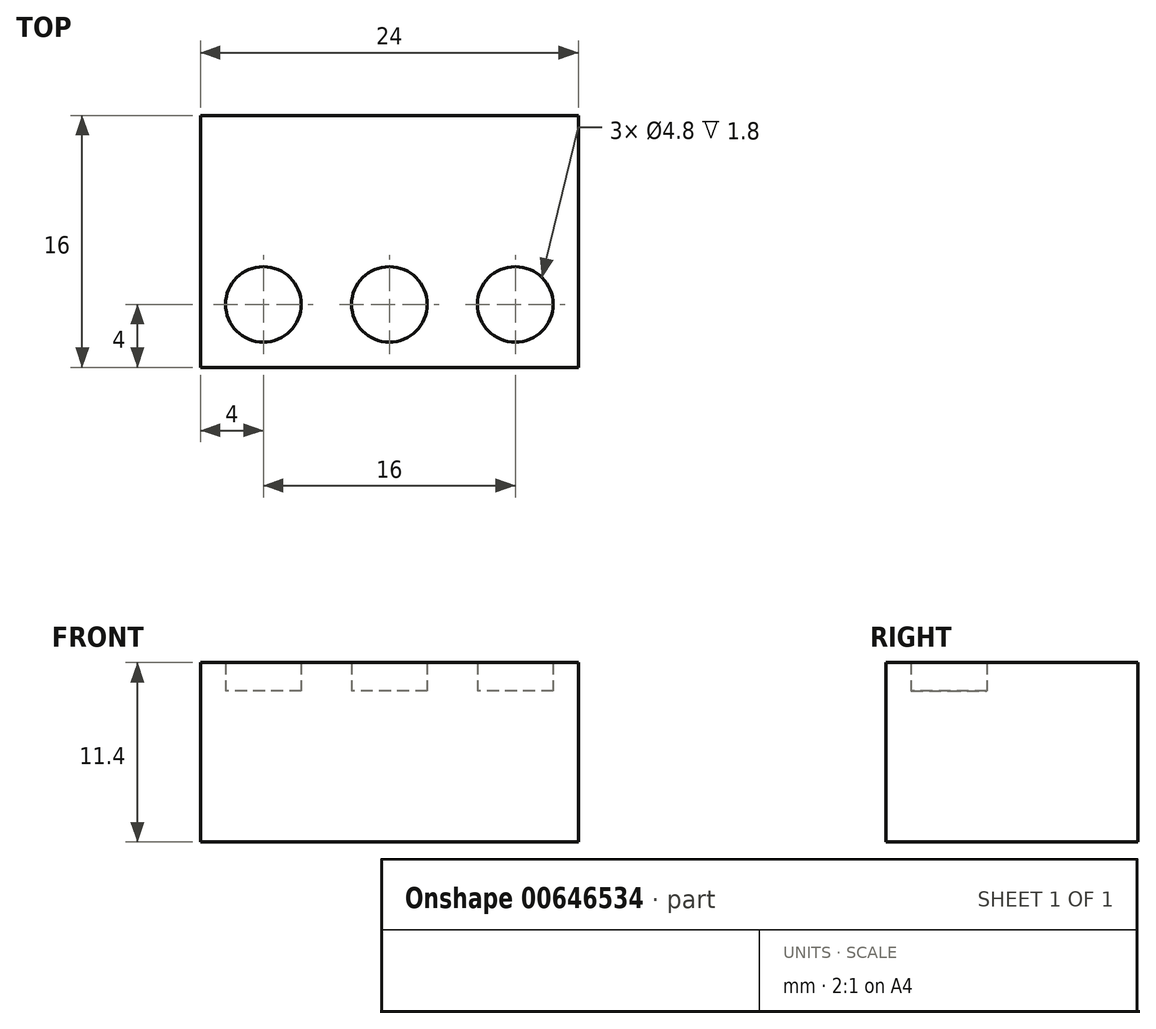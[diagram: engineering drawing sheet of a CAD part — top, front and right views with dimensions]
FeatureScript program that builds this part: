
annotation { "Feature Type Name" : "Feature", "Feature Type Description" : "" }
export const myFeature = defineFeature(function(context is Context, id is Id, definition is map)
    precondition{}
    {
        {
            var Q0;
            Q0=qCreatedBy(makeId("Top.planeOp"),FACE);
            var sketch = newSketch(context, id + "F0", { "sketchPlane" : qUnion([Q0])});
            skLineSegment(sketch, "E0.bottom", {"start": v(0, 0) * mm, "end": v(-24, 0) * mm});
            skLineSegment(sketch, "E0.top", {"start": v(0, 16) * mm, "end": v(-24, 16) * mm});
            skLineSegment(sketch, "E0.left", {"start": v(0, 0) * mm, "end": v(0, 16) * mm});
            skLineSegment(sketch, "E0.right", {"start": v(-24, 0) * mm, "end": v(-24, 16) * mm});
            skSolve(sketch);
        }
        {
            var Q0;
            Q0 = qSketchRegion(id + "F0", true);
            extrude(context, id + "F1", {"entities" : qUnion([Q0]), "depth" : 9.6 * mm, "offsetDistance" : 25.4 * mm});
        }
        {
            var Q0;
            Q0=makeQuery(id+"F1.opExtrude","CAP_FACE",FACE,{"disambiguationData":[OSD([sQuery(id+"F0.wireOp",EDGE,"E0.bottom"),sQuery(id+"F0.wireOp",EDGE,"E0.top"),sQuery(id+"F0.wireOp",EDGE,"E0.left"),sQuery(id+"F0.wireOp",EDGE,"E0.right")])],"isStart":false});
            var sketch = newSketch(context, id + "F2", { "sketchPlane" : qUnion([Q0])});
            skLineSegment(sketch, "E1", {"start": v(-24, 8) * mm, "end": v(0, 8) * mm, "construction": true});
            skLineSegment(sketch, "E2", {"start": v(-16, 16) * mm, "end": v(-16, 0) * mm, "construction": true});
            skLineSegment(sketch, "E3", {"start": v(-8, 16) * mm, "end": v(-8, 0) * mm, "construction": true});
            skLineSegment(sketch, "E4", {"start": v(-24, 16) * mm, "end": v(-16, 8) * mm, "construction": true});
            skLineSegment(sketch, "E5", {"start": v(-16, 8) * mm, "end": v(-8, 16) * mm, "construction": true});
            skLineSegment(sketch, "E6", {"start": v(-8, 16) * mm, "end": v(0, 8) * mm, "construction": true});
            skCircle(sketch, "E7", {"center": v(-20, 12) * mm, "radius": 2.4 * mm});
            skCircle(sketch, "E8", {"center": v(-12, 12) * mm, "radius": 2.4 * mm});
            skCircle(sketch, "E9", {"center": v(-4, 12) * mm, "radius": 2.4 * mm});
            skCircle(sketch, "E10.MirrorC", {"center": v(-20, 4) * mm, "radius": 2.4 * mm});
            skCircle(sketch, "E11.MirrorC", {"center": v(-12, 4) * mm, "radius": 2.4 * mm});
            skCircle(sketch, "E12.MirrorC", {"center": v(-4, 4) * mm, "radius": 2.4 * mm});
            skSolve(sketch);
        }
        {
            var Q0;
            Q0=makeQuery(id+"F2.imprint","IMPRINT",FACE,{"disambiguationData":[TD([[makeQuery(id+"F2.imprint","IMPRINT",EDGE,{"derivedFrom":sQuery(id+"F2.wireOp",EDGE,"E7")}),1.0]])]});
            var Q1;
            Q1=makeQuery(id+"F2.imprint","IMPRINT",FACE,{"disambiguationData":[TD([[makeQuery(id+"F2.imprint","IMPRINT",EDGE,{"derivedFrom":sQuery(id+"F2.wireOp",EDGE,"E8")}),1.0]])]});
            var Q2;
            Q2=makeQuery(id+"F2.imprint","IMPRINT",FACE,{"disambiguationData":[TD([[makeQuery(id+"F2.imprint","IMPRINT",EDGE,{"derivedFrom":sQuery(id+"F2.wireOp",EDGE,"E9")}),1.0]])]});
            var Q3;
            Q3=makeQuery(id+"F2.imprint","IMPRINT",FACE,{"disambiguationData":[TD([[makeQuery(id+"F2.imprint","IMPRINT",EDGE,{"derivedFrom":sQuery(id+"F2.wireOp",EDGE,"E11.MirrorC")}),-1.0]])]});
            var Q4;
            Q4=makeQuery(id+"F2.imprint","IMPRINT",FACE,{"disambiguationData":[TD([[makeQuery(id+"F2.imprint","IMPRINT",EDGE,{"derivedFrom":sQuery(id+"F2.wireOp",EDGE,"E12.MirrorC")}),-1.0]])]});
            var Q5;
            Q5=makeQuery(id+"F2.imprint","IMPRINT",FACE,{"disambiguationData":[TD([[makeQuery(id+"F2.imprint","IMPRINT",EDGE,{"derivedFrom":sQuery(id+"F2.wireOp",EDGE,"E10.MirrorC")}),-1.0]])]});
            extrude(context, id + "F3", {"entities" : qUnion([Q0, Q1, Q2, Q3, Q4, Q5]), "operationType" : NewBodyOperationType.ADD, "depth" : 1.8 * mm, "offsetDistance" : 25.4 * mm});
        }
    });
